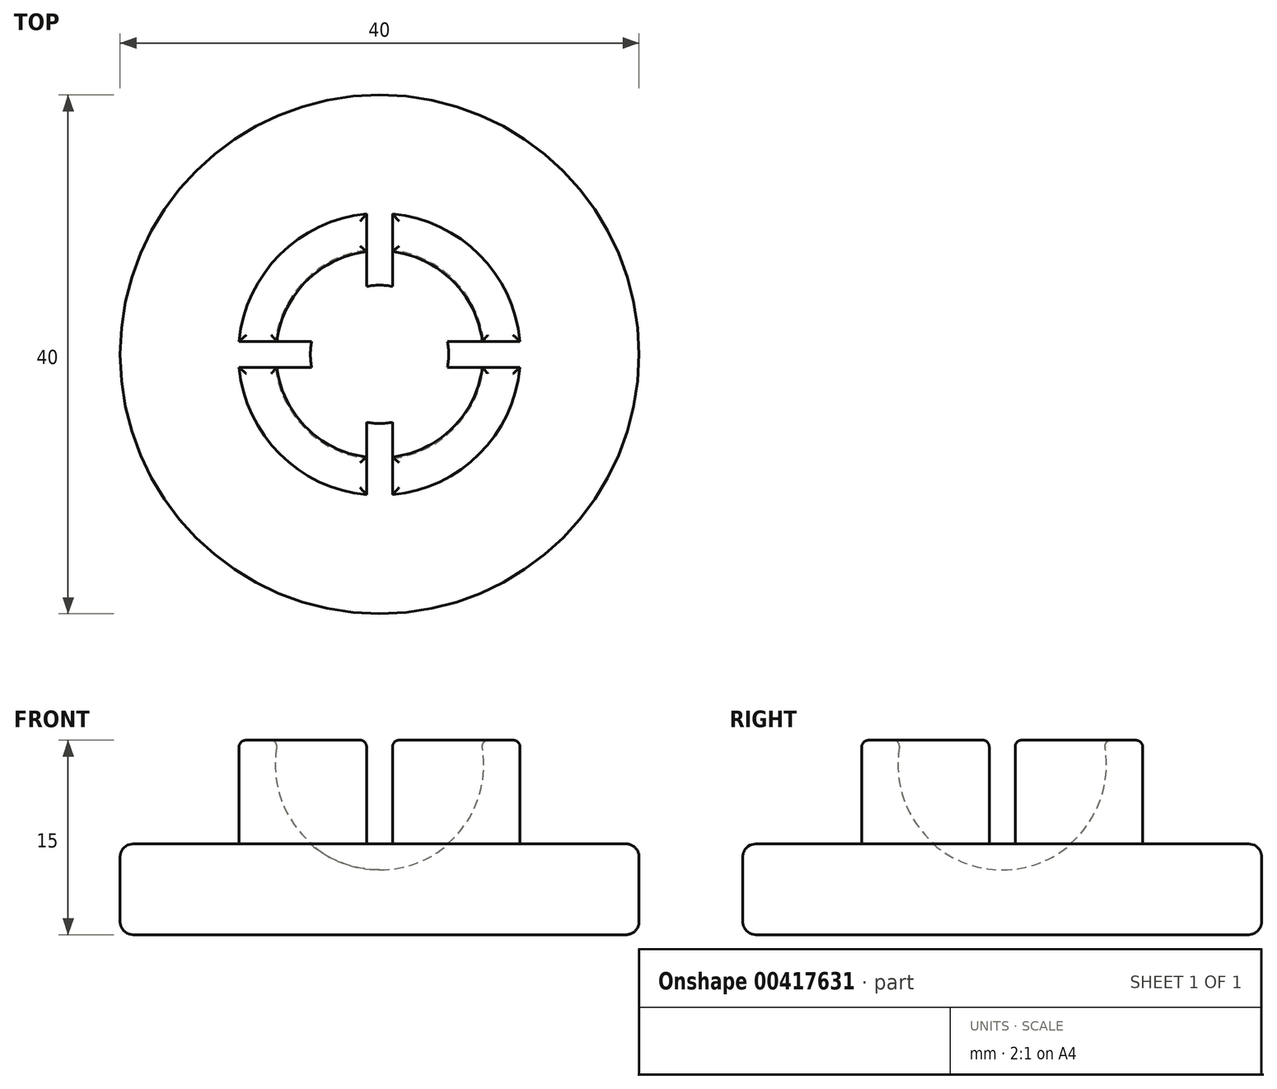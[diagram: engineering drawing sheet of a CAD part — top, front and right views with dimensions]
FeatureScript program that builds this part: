
annotation { "Feature Type Name" : "Feature", "Feature Type Description" : "" }
export const myFeature = defineFeature(function(context is Context, id is Id, definition is map)
    precondition{}
    {
        {
            var Q0;
            Q0=qCreatedBy(makeId("Top.planeOp"),FACE);
            var sketch = newSketch(context, id + "F0", { "sketchPlane" : qUnion([Q0])});
            skCircle(sketch, "E0", {"center": v(0, 0) * mm, "radius": 20 * mm});
            skSolve(sketch);
        }
        {
            var Q0;
            Q0 = qSketchRegion(id + "F0", true);
            extrude(context, id + "F1", {"entities" : qUnion([Q0]), "depth" : 15 * mm});
        }
        {
            var Q0;
            Q0=qCreatedBy(makeId("Front.planeOp"),FACE);
            var sketch = newSketch(context, id + "F2", { "sketchPlane" : qUnion([Q0])});
            skArc(sketch, "E1", {"start": v(0, 5) * mm, "mid": v(8.1, 13.1) * mm, "end": v(0, 21.2) * mm});
            skLineSegment(sketch, "E2", {"start": v(0, 5) * mm, "end": v(0, 21.2) * mm});
            skSolve(sketch);
        }
        {
            var Q0;
            Q0 = qSketchRegion(id + "F2", true);
            var Q1;
            Q1=sQuery(id+"F2.wireOp",EDGE,"E2");
            revolve(context, id + "F3", {"operationType" : NewBodyOperationType.REMOVE, "entities" : qUnion([Q0]), "axis" : qUnion([Q1]), "revolveType" : RevolveType.FULL, "oppositeDirection" : true});
        }
        {
            var Q0;
            Q0=makeQuery(id+"F1.opExtrude","CAP_FACE",FACE,{"disambiguationData":[OSD([sQuery(id+"F0.wireOp",EDGE,"E0")])],"isStart":false});
            var sketch = newSketch(context, id + "F4", { "sketchPlane" : qUnion([Q0])});
            skCircle(sketch, "E3", {"center": v(0, 0) * mm, "radius": 10.87 * mm});
            skCircle(sketch, "E4.0", {"center": v(0, 0) * mm, "radius": 20 * mm});
            skSolve(sketch);
        }
        {
            var Q0;
            Q0 = qSketchRegion(id + "F4", true);
            extrude(context, id + "F5", {"entities" : qUnion([Q0]), "operationType" : NewBodyOperationType.REMOVE, "oppositeDirection" : true, "depth" : 8 * mm});
        }
        {
            var Q0;
            Q0=qCreatedBy(makeId("Front.planeOp"),FACE);
            var sketch = newSketch(context, id + "F6", { "sketchPlane" : qUnion([Q0])});
            skLineSegment(sketch, "E5.bottom", {"start": v(-1, 15) * mm, "end": v(1, 15) * mm});
            skLineSegment(sketch, "E5.top", {"start": v(-1, 7) * mm, "end": v(1, 7) * mm});
            skLineSegment(sketch, "E5.left", {"start": v(-1, 15) * mm, "end": v(-1, 7) * mm});
            skLineSegment(sketch, "E5.right", {"start": v(1, 15) * mm, "end": v(1, 7) * mm});
            skLineSegment(sketch, "E6", {"start": v(0, 0) * mm, "end": v(0, 7) * mm, "construction": true});
            skSolve(sketch);
        }
        {
            var Q0;
            Q0 = qSketchRegion(id + "F6", true);
            extrude(context, id + "F7", {"entities" : qUnion([Q0]), "operationType" : NewBodyOperationType.REMOVE, "endBound" : BoundingType.THROUGH_ALL, "oppositeDirection" : true, "depth" : 25 * mm, "hasSecondDirection" : true, "secondDirectionBound" : SecondDirectionBoundingType.THROUGH_ALL, "secondDirectionOppositeDirection" : false, "secondDirectionDepth" : 25 * mm});
        }
        {
            var Q0;
            Q0=qCreatedBy(makeId("Right.planeOp"),FACE);
            var sketch = newSketch(context, id + "F8", { "sketchPlane" : qUnion([Q0])});
            skLineSegment(sketch, "E7.bottom", {"start": v(-1, 15) * mm, "end": v(1, 15) * mm});
            skLineSegment(sketch, "E7.top", {"start": v(-1, 7) * mm, "end": v(1, 7) * mm});
            skLineSegment(sketch, "E7.left", {"start": v(-1, 15) * mm, "end": v(-1, 7) * mm});
            skLineSegment(sketch, "E7.right", {"start": v(1, 15) * mm, "end": v(1, 7) * mm});
            skLineSegment(sketch, "E8", {"start": v(0, 0) * mm, "end": v(0, 7) * mm, "construction": true});
            skSolve(sketch);
        }
        {
            var Q0;
            Q0 = qSketchRegion(id + "F8", true);
            extrude(context, id + "F9", {"entities" : qUnion([Q0]), "operationType" : NewBodyOperationType.REMOVE, "endBound" : BoundingType.THROUGH_ALL, "oppositeDirection" : true, "depth" : 25 * mm, "hasSecondDirection" : true, "secondDirectionBound" : SecondDirectionBoundingType.THROUGH_ALL, "secondDirectionOppositeDirection" : false, "secondDirectionDepth" : 25 * mm});
        }
        {
            var Q0;
            {var subQ1=makeQuery(id+"F7.opExtrude","SWEPT_FACE",FACE,{"disambiguationData":[OSD([sQuery(id+"F6.wireOp",EDGE,"E5.left")])]});Q0=makeQuery(id+"F9.boolean.opBoolean","SPLIT",FACE,{"disambiguationData":[TD([makeQuery(id+"F7.boolean.opBoolean","COPY",FACE,{"disambiguationData":[OD(1.0)],"derivedFrom":subQ1})])],"derivedFrom":makeQuery(id+"F7.boolean.opBoolean","SPLIT",FACE,{"disambiguationData":[TD([subQ1])],"derivedFrom":makeQuery(id+"F1.opExtrude","CAP_FACE",FACE,{"disambiguationData":[OSD([sQuery(id+"F0.wireOp",EDGE,"E0")])],"isStart":false})})});}
            var Q1;
            {var subQ2=makeQuery(id+"F7.opExtrude","SWEPT_FACE",FACE,{"disambiguationData":[OSD([sQuery(id+"F6.wireOp",EDGE,"E5.right")])]});Q1=makeQuery(id+"F9.boolean.opBoolean","SPLIT",FACE,{"disambiguationData":[TD([makeQuery(id+"F7.boolean.opBoolean","COPY",FACE,{"disambiguationData":[OD(1.0)],"derivedFrom":subQ2})])],"derivedFrom":makeQuery(id+"F7.boolean.opBoolean","SPLIT",FACE,{"disambiguationData":[TD([subQ2])],"derivedFrom":makeQuery(id+"F1.opExtrude","CAP_FACE",FACE,{"disambiguationData":[OSD([sQuery(id+"F0.wireOp",EDGE,"E0")])],"isStart":false})})});}
            var Q2;
            {var subQ2=makeQuery(id+"F7.opExtrude","SWEPT_FACE",FACE,{"disambiguationData":[OSD([sQuery(id+"F6.wireOp",EDGE,"E5.right")])]});Q2=makeQuery(id+"F9.boolean.opBoolean","SPLIT",FACE,{"disambiguationData":[TD([makeQuery(id+"F7.boolean.opBoolean","COPY",FACE,{"disambiguationData":[OD(0.0)],"derivedFrom":subQ2})])],"derivedFrom":makeQuery(id+"F7.boolean.opBoolean","SPLIT",FACE,{"disambiguationData":[TD([subQ2])],"derivedFrom":makeQuery(id+"F1.opExtrude","CAP_FACE",FACE,{"disambiguationData":[OSD([sQuery(id+"F0.wireOp",EDGE,"E0")])],"isStart":false})})});}
            var Q3;
            {var subQ2=makeQuery(id+"F7.opExtrude","SWEPT_FACE",FACE,{"disambiguationData":[OSD([sQuery(id+"F6.wireOp",EDGE,"E5.left")])]});Q3=makeQuery(id+"F9.boolean.opBoolean","SPLIT",FACE,{"disambiguationData":[TD([makeQuery(id+"F7.boolean.opBoolean","COPY",FACE,{"disambiguationData":[OD(0.0)],"derivedFrom":subQ2})])],"derivedFrom":makeQuery(id+"F7.boolean.opBoolean","SPLIT",FACE,{"disambiguationData":[TD([subQ2])],"derivedFrom":makeQuery(id+"F1.opExtrude","CAP_FACE",FACE,{"disambiguationData":[OSD([sQuery(id+"F0.wireOp",EDGE,"E0")])],"isStart":false})})});}
            fillet(context, id + "F10", {"entities" : qUnion([Q0, Q1, Q2, Q3]), "radius" : 0.5 * mm, "tangentPropagation" : true, "allowEdgeOverflow" : false});
        }
        {
            var Q0;
            Q0=makeQuery(id+"F1.opExtrude","SWEPT_FACE",FACE,{"disambiguationData":[OSD([sQuery(id+"F0.wireOp",EDGE,"E0")])]});
            fillet(context, id + "F11", {"entities" : qUnion([Q0]), "radius" : 1 * mm, "tangentPropagation" : true, "allowEdgeOverflow" : false});
        }
    });
